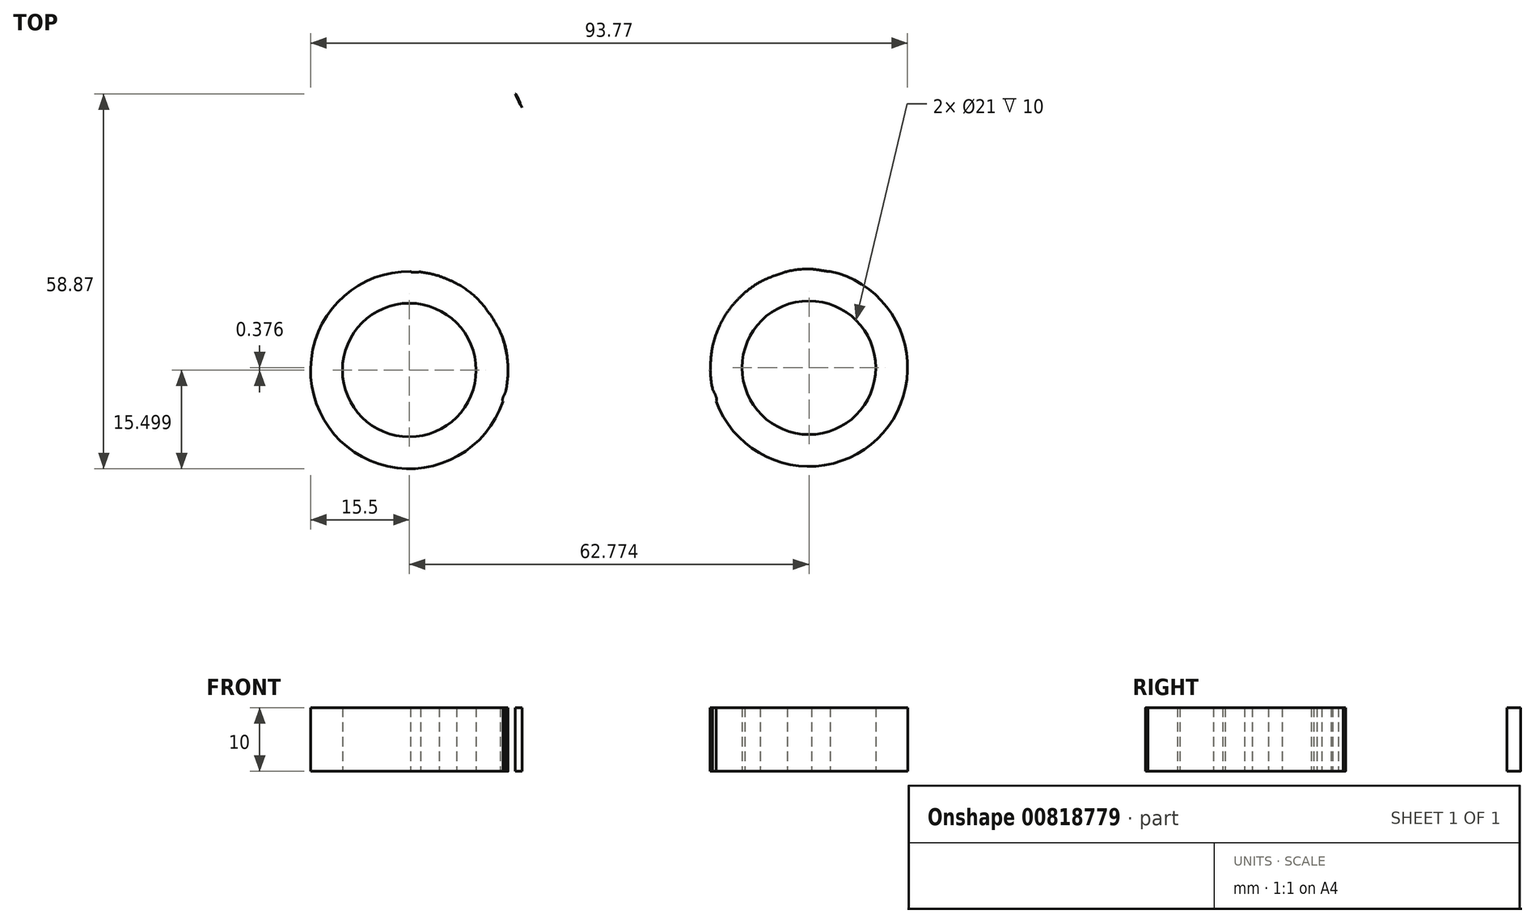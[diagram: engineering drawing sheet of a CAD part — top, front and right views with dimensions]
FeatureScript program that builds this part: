
annotation { "Feature Type Name" : "Feature", "Feature Type Description" : "" }
export const myFeature = defineFeature(function(context is Context, id is Id, definition is map)
    precondition{}
    {
        {
            var Q0;
            Q0=qCreatedBy(makeId("Top.planeOp"),FACE);
            var sketch = newSketch(context, id + "F0", { "sketchPlane" : qUnion([Q0])});
            skCircle(sketch, "E0", {"center": v(0, 0) * mm, "radius": 10.5 * mm});
            skCircle(sketch, "E1", {"center": v(0, 33.65) * mm, "radius": 10.5 * mm});
            skCircle(sketch, "E2", {"center": v(31.76, -15.18) * mm, "radius": 10.5 * mm});
            skCircle(sketch, "E3", {"center": v(-31, -15.55) * mm, "radius": 10.5 * mm});
            skCircle(sketch, "E4", {"center": v(-31, -15.55) * mm, "radius": 15.5 * mm});
            skCircle(sketch, "E5", {"center": v(0, 0) * mm, "radius": 15.5 * mm});
            skCircle(sketch, "E6", {"center": v(31.76, -15.18) * mm, "radius": 15.5 * mm});
            skCircle(sketch, "E7", {"center": v(0, 33.65) * mm, "radius": 15.5 * mm});
            skPoint(sketch, "E8.23.internal.snap0", {"position": v(0.44, -20.45) * mm});
            skFitSpline(sketch, "E8", {"points": [v(-30.8, -0.05) * mm, v(-18.19, 12.74) * mm, v(-14.36, 27.82) * mm, v(-13.28, 25.66) * mm, v(-10.75, 22.49) * mm, v(-5.16, 19.03) * mm, v(2.16, 18.3) * mm, v(8.42, 20.63) * mm, v(13.08, 25.33) * mm, v(14.36, 27.82) * mm, v(19.81, 12.85) * mm, v(35.1, 0) * mm, v(32.2, 0.32) * mm, v(29.59, 0.17) * mm, v(28.36, -0.05) * mm, v(24.08, -1.71) * mm, v(21.7, -3.38) * mm, v(19.7, -5.45) * mm, v(17.87, -8.3) * mm, v(16.64, -11.8) * mm, v(16.27, -15.55) * mm, v(16.64, -18.55) * mm, v(17.19, -20.45) * mm, v(0, -20.45) * mm, v(-16.3, -20.45) * mm, v(-15.9, -18.97) * mm, v(-15.56, -14.33) * mm, v(-16.69, -9.62) * mm, v(-20.51, -4.15) * mm, v(-23.58, -1.95) * mm, v(-26.33, -0.77) * mm, v(-29.25, -0.15) * mm, v(-30.8, -0.05) * mm]});
            skSolve(sketch);
        }
        {
            var Q0;
            {var subQ0=sQuery(id+"F0.wireOp",EDGE,"E8");var subQ13=sQuery(id+"F0.wireOp",EDGE,"E4");var subQ22=makeQuery(id+"F0.imprint","INTERSECT",VERTEX,{"disambiguationData":[OD(2.0)],"derivedFrom":[subQ13,subQ0]});Q0=makeQuery(id+"F0.imprint","IMPRINT",FACE,{"disambiguationData":[TD([[makeQuery(id+"F0.imprint","IMPRINT",EDGE,{"disambiguationData":[TD([[subQ22,-1.0]])],"derivedFrom":subQ13}),-1.0]])]});}
            extrude(context, id + "F1", {"entities" : qUnion([Q0]), "depth" : 10 * mm, "offsetDistance" : 25 * mm});
        }
        {
            var Q0;
            {var subQ0=sQuery(id+"F0.wireOp",EDGE,"E8");var subQ1=sQuery(id+"F0.wireOp",EDGE,"E7");var subQ8=makeQuery(id+"F0.imprint","INTERSECT",VERTEX,{"disambiguationData":[OD(0.0)],"derivedFrom":[subQ1,subQ0]});Q0=makeQuery(id+"F0.imprint","IMPRINT",FACE,{"disambiguationData":[TD([[makeQuery(id+"F0.imprint","IMPRINT",EDGE,{"disambiguationData":[TD([[subQ8,-1.0]])],"derivedFrom":subQ1}),1.0]])]});}
            var Q1;
            Q1=makeQuery(id+"F0.imprint","IMPRINT",FACE,{"disambiguationData":[TD([[makeQuery(id+"F0.imprint","IMPRINT",EDGE,{"derivedFrom":sQuery(id+"F0.wireOp",EDGE,"E3")}),-1.0]])]});
            var Q2;
            {var subQ0=sQuery(id+"F0.wireOp",EDGE,"E8");var subQ1=sQuery(id+"F0.wireOp",EDGE,"E6");var subQ11=makeQuery(id+"F0.imprint","INTERSECT",VERTEX,{"disambiguationData":[OD(0.0)],"derivedFrom":[subQ1,subQ0]});Q2=makeQuery(id+"F0.imprint","IMPRINT",FACE,{"disambiguationData":[TD([[makeQuery(id+"F0.imprint","IMPRINT",EDGE,{"disambiguationData":[TD([[subQ11,1.0]])],"derivedFrom":subQ1}),1.0]])]});}
            var Q3;
            Q3=makeQuery(id+"F0.imprint","IMPRINT",FACE,{"disambiguationData":[TD([[makeQuery(id+"F0.imprint","IMPRINT",EDGE,{"derivedFrom":sQuery(id+"F0.wireOp",EDGE,"E3")}),1.0]])]});
            extrude(context, id + "F2", {"entities" : qUnion([Q0, Q1, Q2, Q3]), "depth" : 10 * mm, "offsetDistance" : 25 * mm});
        }
        {
            var Q0;
            Q0=sQuery(id+"F0.wireOp",VERTEX,"E7.center");
            var Q1;
            Q1=sQuery(id+"F0.wireOp",VERTEX,"E0.center");
            var Q2;
            Q2=sQuery(id+"F0.wireOp",VERTEX,"E6.center");
            var Q3;
            Q3=sQuery(id+"F0.wireOp",VERTEX,"E4.center");
            var Q4;
            Q4=makeQuery(id+"F2.opExtrude","SWEPT_BODY",BODY,{"disambiguationData":[OSD([sQuery(id+"F0.wireOp",EDGE,"E7"),sQuery(id+"F0.wireOp",EDGE,"E8")])]});
            var Q5;
            Q5=makeQuery(id+"F1.opExtrude","SWEPT_BODY",BODY,{"disambiguationData":[OSD([sQuery(id+"F0.wireOp",EDGE,"E4"),sQuery(id+"F0.wireOp",EDGE,"E6"),sQuery(id+"F0.wireOp",EDGE,"E7"),sQuery(id+"F0.wireOp",EDGE,"E8")])]});
            var Q6;
            Q6=makeQuery(id+"F2.opExtrude","SWEPT_BODY",BODY,{"disambiguationData":[OSD([sQuery(id+"F0.wireOp",EDGE,"E6"),sQuery(id+"F0.wireOp",EDGE,"E8")])]});
            var Q7;
            Q7=makeQuery(id+"F2.opExtrude","SWEPT_BODY",BODY,{"disambiguationData":[OSD([sQuery(id+"F0.wireOp",EDGE,"E4"),sQuery(id+"F0.wireOp",EDGE,"E8")])]});
            hole(context, id + "F3", {"style" : HoleStyle.SIMPLE, "endStyle" : HoleEndStyle.THROUGH, "oppositeDirection" : true, "holeDiameter" : 21 * mm, "majorDiameter" : 5 * mm, "isTappedThrough" : true, "tappedDepth" : 12 * mm, "tapClearance" : 3, "locations" : qUnion([Q0, Q1, Q2, Q3]), "scope" : qUnion([Q4, Q5, Q6, Q7])});
        }
    });
